# Revit family: Rohrschelle Sigma, M 8, Gummi weiß
name_source: partatom
category: HLS-Bauteile
revit_build: Autodesk Revit 2017 (Build: 20190507_1515(x64)
units: mm (PartAtom-declared; Revit-internal decimal feet)

## family parameters
Arbeitsebenenbasiert = Ja
Beim Laden mit Abzugskörper schneiden = Nein
Bemaßung runder Anschluss = Durchmesser verwenden
Gemeinsam genutzt = Ja
Immer vertikal = Nein
Raumberechnungspunkt = Nein
Teiletyp = Normal

## types (5) — shared parameters
A = 12 mm  [stored 0.0393701 ft]
Anschluss = M8
Anschlußhöhe = 12 mm
Bauart = einteilig
Baustoffklasse = B2
DS = 3 mm  [stored 0.00984252 ft]
DVS = 5 mm  [stored 0.0164042 ft]
Dämmstärke = 3 mm  [stored 0.00984252 ft]
Fabrikat = MEFA
Farbe Schalldämmeinlage = weiß
Firma = MEFA Befestigungs- und Montagesysteme GmbH
HGA = 8 mm  [stored 0.0262467 ft]
Kurztext1 = Rohrschelle Sigma weiß 20x1,0
MB = 20 mm  [stored 0.0656168 ft]
MD = 1 mm  [stored 0.00328084 ft]
Material = Stahl
Material Schalldämmeinlage = EPDM
Materialmaße = 20x1,0 mm
Materialname = DC01-A, DD11
Mengeneinheit = St
Oberflaeche = galvanisch verzinkt
Schalldämmeinlage = Gummi
Verschluss = Sigma Sicherheits-Schnellverschluss
Verschluss-Schraube = M5
Vorgabe-Ansicht = 1219 mm
max. Temperaturbeständigkeit = 100 °C
max. zul. Last = 0.60 kN
max. zul. Last horizontal = 0.00 kN
max. zul. Last vertikal = 0.00 kN
vpe = 100 St
zero-valued in all types: Nennweite DN Rohr, Rohraußendurchmesser, Stärke Material

## per-type parameters (varying)
| type | Artikelnummer | B | Breite | D | D0 | DF1 | DF2 | Dmax | EAN | Gewicht | Gewicht pro Bauteil | H | Kurztext2 | R | RM | Rohraußendurchmesser Zoll | max. Höhe | max. Rohraußendurchmesser | min. Rohraußendurchmesser |
| Sigma, Ø 12- 15, M 8, Gummi weiß | 14590151 | 41 mm  [stored 0.134514 ft] | 41 mm  [stored 0.134514 ft] | 15 mm  [stored 0.0492126 ft] | 21 mm | 19 mm  [stored 0.062336 ft] | 7 mm  [stored 0.0229659 ft] | 15 mm  [stored 0.0492126 ft] | 4250928432391 | 0.03 kg | 0.03 kg | 31 mm  [stored 0.101706 ft] | 12 - 15 mm M8 EPDM | 11 mm | 12 mm  [stored 0.0393701 ft] | 1/4 Zoll | 33 mm  [stored 0.108268 ft] | 15 mm  [stored 0.0492126 ft] | 12 mm  [stored 0.0393701 ft] |
| Sigma, Ø 16- 19, M 8, Gummi weiß | 14590191 | 45 mm  [stored 0.147638 ft] | 45 mm  [stored 0.147638 ft] | 19 mm  [stored 0.062336 ft] | 25 mm  [stored 0.082021 ft] | 19 mm  [stored 0.062336 ft] | 7 mm  [stored 0.0229659 ft] | 19 mm  [stored 0.062336 ft] | 4250928432407 | 0.03 kg | 0.03 kg | 35 mm  [stored 0.114829 ft] | 16 - 19 mm M8 EPDM | 13 mm | 14 mm  [stored 0.0459318 ft] | 3/8 Zoll | 37 mm  [stored 0.121391 ft] | 19 mm  [stored 0.062336 ft] | 16 mm  [stored 0.0524934 ft] |
| Sigma, Ø 25- 29, M 8, Gummi weiß | 14590291 | 56 mm  [stored 0.183727 ft] | 56 mm  [stored 0.183727 ft] | 29 mm  [stored 0.0951444 ft] | 35 mm  [stored 0.114829 ft] | 19 mm  [stored 0.062336 ft] | 8 mm  [stored 0.0262467 ft] | 29 mm  [stored 0.0951444 ft] | 4250928432421 | 0.04 kg | 0.04 kg | 45 mm  [stored 0.147638 ft] | 25 - 29 mm M8 EPDM | 18 mm  [stored 0.0590551 ft] | 19 mm  [stored 0.062336 ft] | 3/4 Zoll | 47 mm  [stored 0.154199 ft] | 29 mm  [stored 0.0951444 ft] | 25 mm  [stored 0.082021 ft] |
| Sigma, Ø 32- 35, M 8, Gummi weiß | 14590351 | 62 mm  [stored 0.203412 ft] | 62 mm  [stored 0.203412 ft] | 35 mm  [stored 0.114829 ft] | 41 mm  [stored 0.134514 ft] | 19 mm  [stored 0.062336 ft] | 8 mm  [stored 0.0262467 ft] | 35 mm  [stored 0.114829 ft] | 4250928432438 | 0.04 kg | 0.04 kg | 51 mm | 32 - 35 mm M8 EPDM | 21 mm | 22 mm | 1 Zoll | 53 mm  [stored 0.173885 ft] | 35 mm  [stored 0.114829 ft] | 32 mm  [stored 0.104987 ft] |
| Sigma, Ø 20- 23, M 8, Gummi weiß | 14590231 | 51 mm | 51 mm | 23 mm  [stored 0.0754593 ft] | 29 mm  [stored 0.0951444 ft] | 20 mm  [stored 0.0656168 ft] | 8 mm  [stored 0.0262467 ft] | 23 mm  [stored 0.0754593 ft] | 4250928432414 | 0.03 kg | 0.03 kg | 39 mm  [stored 0.127953 ft] | 20 - 23 mm M8 EPDM | 15 mm  [stored 0.0492126 ft] | 16 mm  [stored 0.0524934 ft] | 1/2 Zoll | 41 mm  [stored 0.134514 ft] | 23 mm  [stored 0.0754593 ft] | 20 mm  [stored 0.0656168 ft] |

note: [stored X ft] marks values corroborated as IEEE doubles in the binary element streams (Revit-internal decimal feet)

## geometry (parser evidence)
native form markers: Sweep x3
no freeform markers — native parametric forms only
